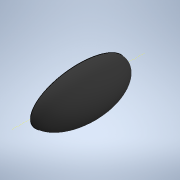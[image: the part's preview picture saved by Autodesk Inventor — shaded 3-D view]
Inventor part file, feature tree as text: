
AUTODESK INVENTOR PART (.ipt)
format: ipt  version: 2022 (Build 260153000, 153)  size: 149,504 bytes
history: native  units: mm
features: revolve x1, sketch x1
ambient origin geometry x8: Origin, YZ Plane, XZ Plane, XY Plane, X Axis, Y Axis, Z Axis, Center Point
bodies: Solid1 (feature_tree)
feature tree (2):
  revolve  "Revolution1"  [1 undecoded]
  sketch  "Sketch1"  dims[d0=50.0mm d1=50.0mm d3=180.0deg d5=50.0mm d6=25.0mm]
note: 1 required parameter value undecoded (feature->parameter linkage not recoverable at this tier; creation-order binding heuristic only, values carry confidence <= 0.55)
